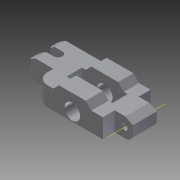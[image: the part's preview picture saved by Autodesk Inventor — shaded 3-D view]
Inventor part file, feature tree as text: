
AUTODESK INVENTOR PART (.ipt)
format: ipt  version: 2012 (Build 160160000, 160)  size: 187,392 bytes
history: native  units: mm
features: extrude x6, sketch x6, hole x3, chamfer x3, fillet x2, other x1
ambient origin geometry x8: Origin, YZ Plane, XZ Plane, XY Plane, X Axis, Y Axis, Z Axis, Center Point
bodies: Solid1 (feature_tree)
feature tree (21):
  extrude  "Extrusion1"  Depth=35.0mm
  hole  "Hole1"  [1 undecoded]
  chamfer  "Chamfer1"  Distance=10.0mm
  other  "Work Axis1"
  hole  "Hole2"  [1 undecoded]
  extrude  "Extrusion2"  Depth=20.0mm
  chamfer  "Chamfer2"  Distance=3.0mm
  extrude  "Extrusion3"  Depth=3.0mm TaperAngle=45.0deg
  hole  "Hole3"  [1 undecoded]
  extrude  "Extrusion4"  Depth=13.0mm TaperAngle=0.0deg
  fillet  "Fillet1"  Radius=10.0mm
  extrude  "Extrusion5"  Depth=2.0mm
  fillet  "Fillet2"  Radius=10.0mm
  extrude  "Extrusion6"  Depth=3.555603mm
  chamfer  "Chamfer3"  Distance=2.201481mm
  sketch  "Sketch1"  dims[d0=25.0mm d1=35.0mm]
  sketch  "Sketch2"  dims[d2=12.5mm d3=6.25mm]
  sketch  "Sketch3"  dims[d4=9.5mm d5=10.0mm d6=0.0mm]
  sketch  "Sketch4"  dims[d7=5.0mm d8=5.2mm d9=3.0mm d10=6.0mm d11=4.0mm d12=2.0mm d13=90.0deg d14=1.0mm d15=20.594885mm d16=2.5mm d17=2.0mm d18=45.0deg]
  sketch  "Sketch5"  dims[d19=4.51mm d20=16.0mm d21=8.2mm d22=6.0mm d23=4.0mm d24=2.0mm d25=90.0deg d26=1.0mm d27=20.594885mm d28=20.0mm]
  sketch  "Sketch6"  dims[d29=6.0mm d30=3.0mm d31=0.0mm d32=3.0mm d33=2.0mm d34=45.0deg d35=16.0mm d36=13.0mm d37=0.0mm d38=8.0mm d39=7.5mm d40=4.5mm d41=6.0mm d42=4.0mm d43=2.0mm d44=90.0deg d45=1.0mm d46=20.594885mm d47=10.0mm d48=0.0mm d49=2.0mm d50=10.0mm d51=0.0mm d52=3.555603mm d53=2.201481mm d54=6.0mm d55=24.0mm d56=8.0mm d57=9.0mm d58=7.9mm d61=10.0mm d62=0.0mm d63=2.0mm d64=4.0mm d65=45.0deg d66=1.0mm d67=1.0mm]
note: 3 required parameter values undecoded (feature->parameter linkage not recoverable at this tier; creation-order binding heuristic only, values carry confidence <= 0.55)
